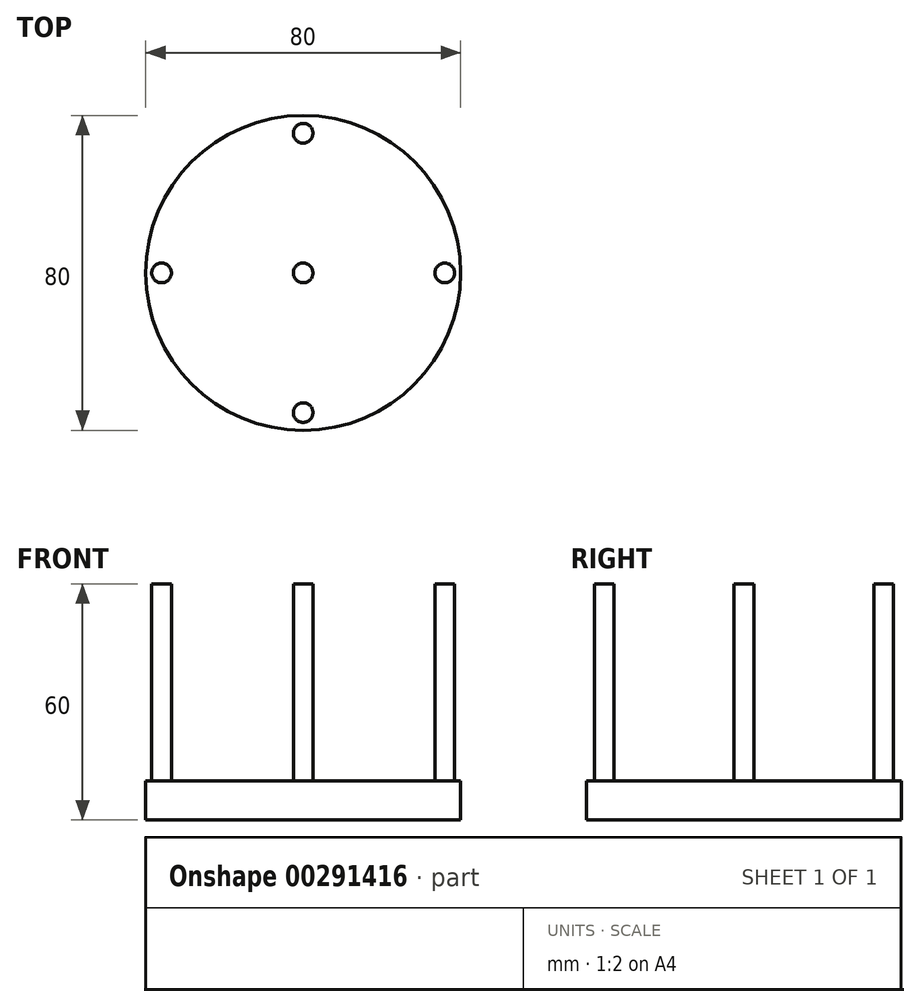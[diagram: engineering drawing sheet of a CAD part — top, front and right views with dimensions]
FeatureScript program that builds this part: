
annotation { "Feature Type Name" : "Feature", "Feature Type Description" : "" }
export const myFeature = defineFeature(function(context is Context, id is Id, definition is map)
    precondition{}
    {
        {
            var Q0;
            Q0=qCreatedBy(makeId("Top.planeOp"),FACE);
            var sketch = newSketch(context, id + "F0", { "sketchPlane" : qUnion([Q0])});
            skCircle(sketch, "E0", {"center": v(0, 0) * mm, "radius": 40 * mm});
            skSolve(sketch);
        }
        {
            var Q0;
            Q0=makeQuery(id+"F0.imprint","IMPRINT",FACE,{"disambiguationData":[TD([[makeQuery(id+"F0.imprint","IMPRINT",EDGE,{"derivedFrom":sQuery(id+"F0.wireOp",EDGE,"E0")}),1.0]])]});
            extrude(context, id + "F1", {"entities" : qUnion([Q0]), "depth" : 10 * mm});
        }
        {
            var Q0;
            Q0=makeQuery(id+"F1.opExtrude","CAP_FACE",FACE,{"disambiguationData":[OSD([sQuery(id+"F0.wireOp",EDGE,"E0")])],"isStart":false});
            var sketch = newSketch(context, id + "F2", { "sketchPlane" : qUnion([Q0])});
            skCircle(sketch, "E1", {"center": v(0, 0) * mm, "radius": 2.5 * mm});
            skSolve(sketch);
        }
        {
            var Q0;
            Q0=makeQuery(id+"F2.imprint","IMPRINT",FACE,{"disambiguationData":[TD([[makeQuery(id+"F2.imprint","IMPRINT",EDGE,{"derivedFrom":sQuery(id+"F2.wireOp",EDGE,"E1")}),1.0]])]});
            extrude(context, id + "F3", {"entities" : qUnion([Q0]), "operationType" : NewBodyOperationType.ADD, "depth" : 50 * mm});
        }
        {
            var Q0;
            Q0=makeQuery(id+"F1.opExtrude","CAP_FACE",FACE,{"disambiguationData":[OSD([sQuery(id+"F0.wireOp",EDGE,"E0")])],"isStart":false});
            var sketch = newSketch(context, id + "F4", { "sketchPlane" : qUnion([Q0])});
            skCircle(sketch, "E2", {"center": v(0, 35.49) * mm, "radius": 2.5 * mm});
            skCircle(sketch, "E3", {"center": v(0, -35.5) * mm, "radius": 2.5 * mm});
            skCircle(sketch, "E4", {"center": v(35.98, 0) * mm, "radius": 2.5 * mm});
            skCircle(sketch, "E5", {"center": v(-35.97, 0) * mm, "radius": 2.5 * mm});
            skSolve(sketch);
        }
        {
            var Q0;
            Q0=makeQuery(id+"F4.imprint","IMPRINT",FACE,{"disambiguationData":[TD([[makeQuery(id+"F4.imprint","IMPRINT",EDGE,{"derivedFrom":sQuery(id+"F4.wireOp",EDGE,"E2")}),1.0]])]});
            var Q1;
            Q1=makeQuery(id+"F4.imprint","IMPRINT",FACE,{"disambiguationData":[TD([[makeQuery(id+"F4.imprint","IMPRINT",EDGE,{"derivedFrom":sQuery(id+"F4.wireOp",EDGE,"E5")}),1.0]])]});
            var Q2;
            Q2=makeQuery(id+"F4.imprint","IMPRINT",FACE,{"disambiguationData":[TD([[makeQuery(id+"F4.imprint","IMPRINT",EDGE,{"derivedFrom":sQuery(id+"F4.wireOp",EDGE,"E3")}),1.0]])]});
            var Q3;
            Q3=makeQuery(id+"F4.imprint","IMPRINT",FACE,{"disambiguationData":[TD([[makeQuery(id+"F4.imprint","IMPRINT",EDGE,{"derivedFrom":sQuery(id+"F4.wireOp",EDGE,"E4")}),1.0]])]});
            extrude(context, id + "F5", {"entities" : qUnion([Q0, Q1, Q2, Q3]), "operationType" : NewBodyOperationType.ADD, "depth" : 50 * mm});
        }
    });
